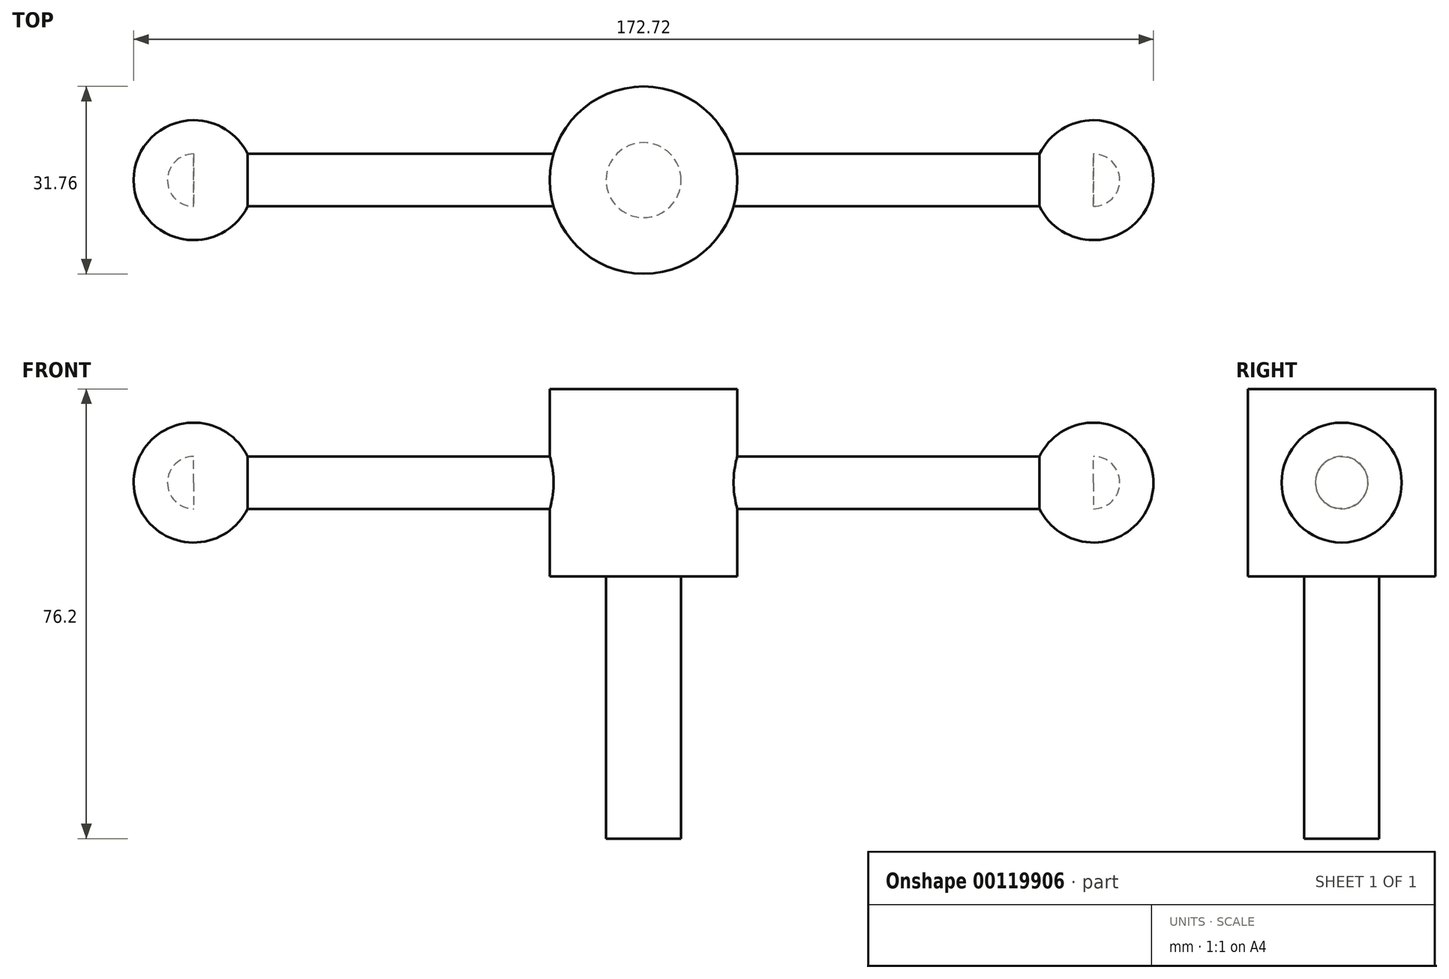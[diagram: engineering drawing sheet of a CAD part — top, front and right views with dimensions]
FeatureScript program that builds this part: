
annotation { "Feature Type Name" : "Feature", "Feature Type Description" : "" }
export const myFeature = defineFeature(function(context is Context, id is Id, definition is map)
    precondition{}
    {
        {
            var Q0;
            Q0=qCreatedBy(makeId("Top.planeOp"),FACE);
            var sketch = newSketch(context, id + "F0", { "sketchPlane" : qUnion([Q0])});
            skCircle(sketch, "E0", {"center": v(0, 0) * mm, "radius": 15.88 * mm});
            skCircle(sketch, "E1", {"center": v(0, 0) * mm, "radius": 6.35 * mm});
            skSolve(sketch);
        }
        {
            var Q0;
            Q0=makeQuery(id+"F0.imprint","IMPRINT",FACE,{"disambiguationData":[TD([[makeQuery(id+"F0.imprint","IMPRINT",EDGE,{"derivedFrom":sQuery(id+"F0.wireOp",EDGE,"E0")}),1.0]])]});
            extrude(context, id + "F1", {"entities" : qUnion([Q0]), "depth" : 31.75 * mm});
        }
        {
            var Q0;
            Q0=makeQuery(id+"F0.imprint","IMPRINT",FACE,{"disambiguationData":[TD([[makeQuery(id+"F0.imprint","IMPRINT",EDGE,{"derivedFrom":sQuery(id+"F0.wireOp",EDGE,"E1")}),1.0]])]});
            extrude(context, id + "F2", {"entities" : qUnion([Q0]), "operationType" : NewBodyOperationType.ADD, "depth" : 31.75 * mm, "hasSecondDirection" : true, "secondDirectionOppositeDirection" : true, "secondDirectionDepth" : 44.45 * mm});
        }
        {
            var Q0;
            Q0=qCreatedBy(makeId("Right.planeOp"),FACE);
            var sketch = newSketch(context, id + "F3", { "sketchPlane" : qUnion([Q0])});
            skLineSegment(sketch, "E2", {"start": v(0, 30.86) * mm, "end": v(0, 0) * mm, "construction": true});
            skLineSegment(sketch, "E3", {"start": v(0, 15.88) * mm, "end": v(-13.68, 15.88) * mm, "construction": true});
            skCircle(sketch, "E4", {"center": v(0, 15.88) * mm, "radius": 4.45 * mm});
            skSolve(sketch);
        }
        {
            var Q0;
            Q0=qSketchRegion(id+"F3",true);
            extrude(context, id + "F4", {"entities" : qUnion([Q0]), "operationType" : NewBodyOperationType.ADD, "depth" : 76.2 * mm, "hasSecondDirection" : true, "secondDirectionOppositeDirection" : true, "secondDirectionDepth" : 76.2 * mm});
        }
        {
            var Q0;
            Q0=makeQuery(id+"F4.opExtrude","CAP_FACE",FACE,{"disambiguationData":[OSD([sQuery(id+"F3.wireOp",EDGE,"E4")])],"isStart":false});
            var sketch = newSketch(context, id + "F5", { "sketchPlane" : qUnion([Q0])});
            skCircle(sketch, "E5", {"center": v(0, 15.88) * mm, "radius": 10.16 * mm});
            skLineSegment(sketch, "E6", {"start": v(-10.16, 15.88) * mm, "end": v(10.16, 15.88) * mm});
            skSolve(sketch);
        }
        {
            var Q0;
            {var subQ0=sQuery(id+"F5.wireOp",EDGE,"E6");var subQ1=sQuery(id+"F5.wireOp",EDGE,"E5");var subQ2=makeQuery(id+"F5.imprint","INTERSECT",VERTEX,{"disambiguationData":[OD(0.0)],"derivedFrom":[subQ1,subQ0]});Q0=makeQuery(id+"F5.imprint","IMPRINT",FACE,{"disambiguationData":[TD([[makeQuery(id+"F5.imprint","IMPRINT",EDGE,{"disambiguationData":[TD([[subQ2,-1.0]])],"derivedFrom":subQ1}),1.0]])]});}
            var Q1;
            {var subQ0=sQuery(id+"F5.wireOp",EDGE,"E6");var subQ1=makeQuery(id+"F4.opExtrude","CAP_EDGE",EDGE,{"disambiguationData":[OSD([sQuery(id+"F3.wireOp",EDGE,"E4")])],"isStart":false});var subQ2=makeQuery(id+"F5.imprint","INTERSECT",VERTEX,{"disambiguationData":[OD(0.0)],"derivedFrom":[subQ1,subQ0]});Q1=makeQuery(id+"F5.imprint","IMPRINT",FACE,{"disambiguationData":[TD([[makeQuery(id+"F5.imprint","IMPRINT",EDGE,{"disambiguationData":[TD([[subQ2,-1.0]])],"derivedFrom":subQ0}),1.0]])]});}
            var Q2;
            {var subQ0=sQuery(id+"F5.wireOp",EDGE,"E6");var subQ1=makeQuery(id+"F4.opExtrude","CAP_EDGE",EDGE,{"disambiguationData":[OSD([sQuery(id+"F3.wireOp",EDGE,"E4")])],"isStart":false});var subQ2=makeQuery(id+"F5.imprint","INTERSECT",VERTEX,{"disambiguationData":[OD(0.0)],"derivedFrom":[subQ1,subQ0]});Q2=makeQuery(id+"F5.imprint","IMPRINT",FACE,{"disambiguationData":[TD([[makeQuery(id+"F5.imprint","IMPRINT",EDGE,{"disambiguationData":[TD([[subQ2,-1.0]])],"derivedFrom":subQ0}),-1.0]])]});}
            var Q3;
            Q3=sQuery(id+"F5.wireOp",EDGE,"E6");
            revolve(context, id + "F6", {"operationType" : NewBodyOperationType.ADD, "entities" : qUnion([Q0, Q1, Q2]), "axis" : qUnion([Q3]), "revolveType" : RevolveType.FULL});
        }
        {
            var Q0;
            Q0=makeQuery(id+"F4.opExtrude","CAP_FACE",FACE,{"disambiguationData":[OSD([sQuery(id+"F3.wireOp",EDGE,"E4")])],"isStart":true});
            var sketch = newSketch(context, id + "F7", { "sketchPlane" : qUnion([Q0])});
            skCircle(sketch, "E7", {"center": v(0, 15.88) * mm, "radius": 10.16 * mm});
            skLineSegment(sketch, "E8", {"start": v(-10.16, 15.88) * mm, "end": v(10.16, 15.88) * mm});
            skSolve(sketch);
        }
        {
            var Q0;
            {var subQ0=sQuery(id+"F7.wireOp",EDGE,"E8");var subQ1=sQuery(id+"F7.wireOp",EDGE,"E7");var subQ2=makeQuery(id+"F7.imprint","INTERSECT",VERTEX,{"disambiguationData":[OD(0.0)],"derivedFrom":[subQ1,subQ0]});Q0=makeQuery(id+"F7.imprint","IMPRINT",FACE,{"disambiguationData":[TD([[makeQuery(id+"F7.imprint","IMPRINT",EDGE,{"disambiguationData":[TD([[subQ2,-1.0]])],"derivedFrom":subQ1}),1.0]])]});}
            var Q1;
            {var subQ0=sQuery(id+"F7.wireOp",EDGE,"E8");var subQ1=makeQuery(id+"F4.opExtrude","CAP_EDGE",EDGE,{"disambiguationData":[OSD([sQuery(id+"F3.wireOp",EDGE,"E4")])],"isStart":true});var subQ2=makeQuery(id+"F7.imprint","INTERSECT",VERTEX,{"disambiguationData":[OD(0.0)],"derivedFrom":[subQ1,subQ0]});Q1=makeQuery(id+"F7.imprint","IMPRINT",FACE,{"disambiguationData":[TD([[makeQuery(id+"F7.imprint","IMPRINT",EDGE,{"disambiguationData":[TD([[subQ2,-1.0]])],"derivedFrom":subQ0}),1.0]])]});}
            var Q2;
            {var subQ0=sQuery(id+"F7.wireOp",EDGE,"E8");var subQ1=makeQuery(id+"F4.opExtrude","CAP_EDGE",EDGE,{"disambiguationData":[OSD([sQuery(id+"F3.wireOp",EDGE,"E4")])],"isStart":true});var subQ2=makeQuery(id+"F7.imprint","INTERSECT",VERTEX,{"disambiguationData":[OD(0.0)],"derivedFrom":[subQ1,subQ0]});Q2=makeQuery(id+"F7.imprint","IMPRINT",FACE,{"disambiguationData":[TD([[makeQuery(id+"F7.imprint","IMPRINT",EDGE,{"disambiguationData":[TD([[subQ2,-1.0]])],"derivedFrom":subQ0}),-1.0]])]});}
            var Q3;
            Q3=sQuery(id+"F7.wireOp",EDGE,"E8");
            revolve(context, id + "F8", {"operationType" : NewBodyOperationType.ADD, "entities" : qUnion([Q0, Q1, Q2]), "axis" : qUnion([Q3]), "revolveType" : RevolveType.FULL});
        }
    });
